# Revit family: BE_66649_de_DE
name_source: partatom
category: Leuchten
revit_build: Autodesk Revit 2015 (Build: 20160512_0715(x64)
units: mm (PartAtom-declared; Revit-internal decimal feet)

## types (6) — shared parameters
AC/DC = AC/DC
Aktualisierung = 2017-02-22T04:16:27
BEGA_Dummy = Nein
BEGA_IES = Ja
BEGA_Intern = Ja
BEGA_Intern_Konstruktion = Ja
BEGA_Intern_an = Ja
BEGA_Intern_aus = Ja
Befestigungsabstand = 92 x 14 mm
Befestigungsbohrung = Ø 5,3 mm
Beschreibung = Wandleuchte
Beschreibung_Sonderanfertigung = Hier können Sie Informationen zur Sonderanfertigung eintragen.
CE_Konformität = ja
Energieeffizienzklasse = LED A++ - A
Farbfilter = 16777215
Farbtemperaturverschiebung bei Dämpfen der Lampe = <Keine Auswahl>
Farbwiedergabeindex = Ra > 80
Frequenz = 0/50-60 Hz
Gewicht = 0.75 kg
Hersteller = BEGA
Lampe = LED 3.2 W
Lastklassifizierung = Beleuchtung
Lebensdauerkriterien = L70 = 50.000 h
Logo = BEGA_Logo.png
Material_02 = BEGA_Oberfläche_Silber_matt
Material_03 = BEGA_Oberfläche_Weiss_matt
Material_06 = BEGA_Oberfläche_Edelstahl_gebürstet
Material_09 = BEGA_Glas_klar
Material_11 = BEGA_Glas_opal
Material_15 = BEGA_Leuchtmedium_matt
Material_17 = BEGA_Reflektor
Neigungswinkel = 0.00°
Produktdatenblatt = http://www.bega.de
Scheinlast = 0 VA
Schutzart = IP 65
Schutzklasse = I
Sonderanfertigung = Nein
Spannung = 240 V
Typenbild = 66649.png
URL = http://www.bega.de
Umgebungstemperatur = 25 °C
zero-valued in all types: Vorgabe-Ansicht

## per-type parameters (varying)
| type | Bestellnummer | Datei für fotometrisches Netz | Farbtemperatur | LED_Modulbezeichnung | Lampenlichtstrom | Leuchtenlichtstrom | M_A | M_G | M_W | Modell |
| BEGA_66649_Grafit_K4 | 66649K4 | BE_66649K4.IES | 4000 K | LED-0123/840 | 270 lm | 152 lm | Nein | Ja | Nein | 66649K4 |
| BEGA_66649_Weiß_K3 | 66649W | BE_66649.IES | 3000 K | LED-0123/830 | 245 lm | 138 lm | Nein | Nein | Ja | 66649W |
| BEGA_66649_Weiß_K4 | 66649WK4 | BE_66649K4.IES | 4000 K | LED-0123/840 | 270 lm | 152 lm | Nein | Nein | Ja | 66649WK4 |
| BEGA_66649_Grafit_K3 | 66649 | BE_66649.IES | 3000 K | LED-0123/830 | 245 lm | 138 lm | Nein | Ja | Nein | 66649 |
| BEGA_66649_Silber_K3 | 66649A | BE_66649.IES | 3000 K | LED-0123/830 | 245 lm | 138 lm | Ja | Nein | Nein | 66649A |
| BEGA_66649_Silber_K4 | 66649AK4 | BE_66649K4.IES | 4000 K | LED-0123/840 | 270 lm | 152 lm | Ja | Nein | Nein | 66649AK4 |
